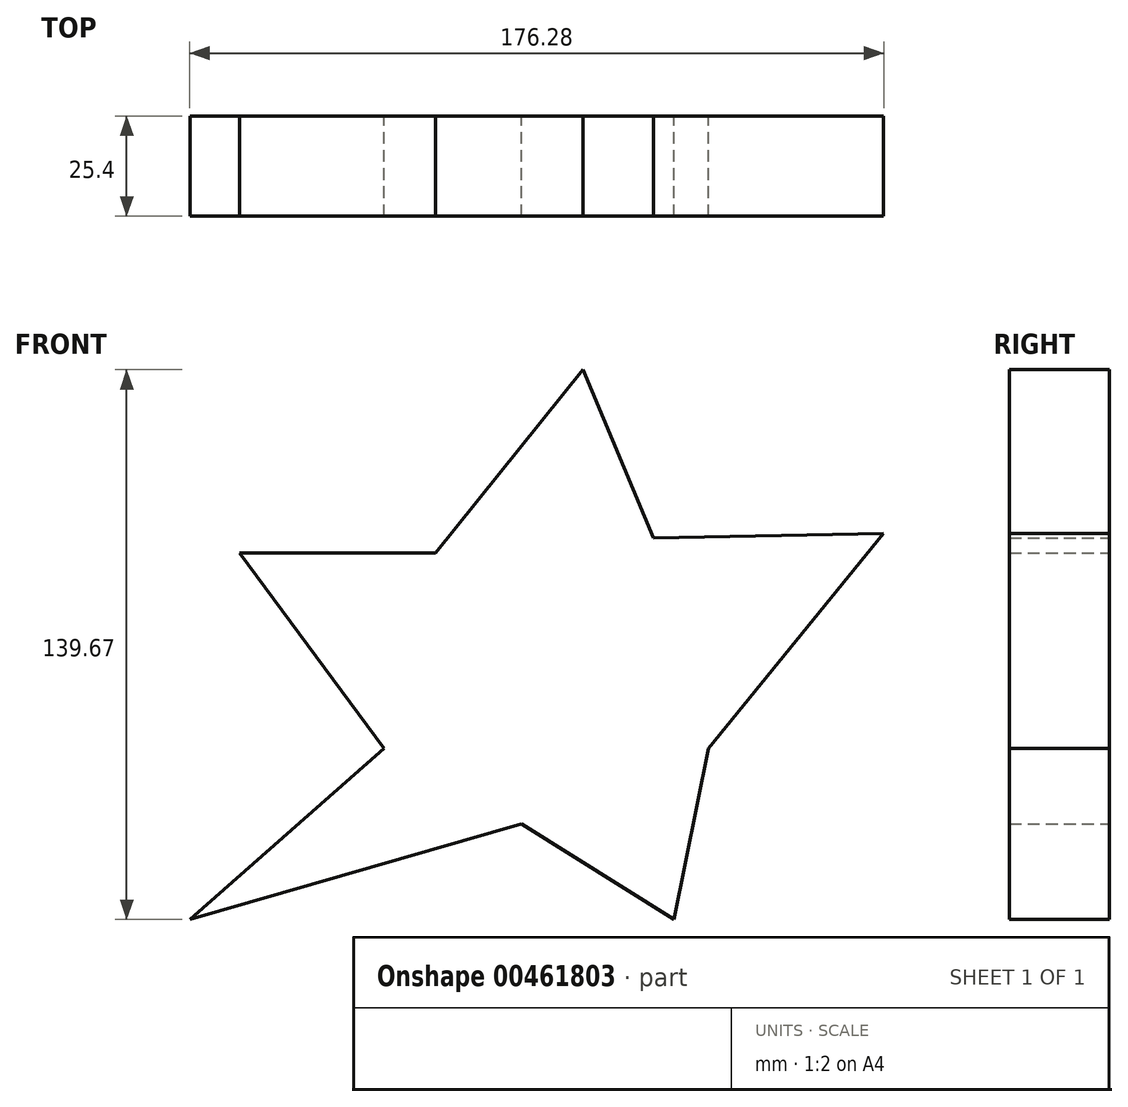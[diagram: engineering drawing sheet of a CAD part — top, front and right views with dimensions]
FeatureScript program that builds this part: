
annotation { "Feature Type Name" : "Feature", "Feature Type Description" : "" }
export const myFeature = defineFeature(function(context is Context, id is Id, definition is map)
    precondition{}
    {
        {
            var Q0;
            Q0=qCreatedBy(makeId("Front.planeOp"),FACE);
            var sketch = newSketch(context, id + "F0", { "sketchPlane" : qUnion([Q0])});
            skLineSegment(sketch, "E0", {"start": v(-36.87, 68.77) * mm, "end": v(-74.4, 22.16) * mm});
            skLineSegment(sketch, "E1", {"start": v(-74.4, 22.16) * mm, "end": v(-124.13, 22.16) * mm});
            skLineSegment(sketch, "E2", {"start": v(-124.13, 22.16) * mm, "end": v(-87.48, -27.44) * mm});
            skLineSegment(sketch, "E3", {"start": v(-87.48, -27.44) * mm, "end": v(-136.79, -70.9) * mm});
            skLineSegment(sketch, "E4", {"start": v(-136.79, -70.9) * mm, "end": v(-52.58, -46.6) * mm});
            skLineSegment(sketch, "E5", {"start": v(-52.58, -46.6) * mm, "end": v(-13.74, -70.9) * mm});
            skLineSegment(sketch, "E6", {"start": v(-13.74, -70.9) * mm, "end": v(-5.02, -27.44) * mm});
            skLineSegment(sketch, "E7", {"start": v(-5.02, -27.44) * mm, "end": v(39.49, 27.1) * mm});
            skLineSegment(sketch, "E8", {"start": v(-18.98, 25.94) * mm, "end": v(39.49, 27.1) * mm});
            skLineSegment(sketch, "E9", {"start": v(-18.98, 25.94) * mm, "end": v(-36.87, 68.77) * mm});
            skSolve(sketch);
        }
        {
            var Q0;
            Q0 = qSketchRegion(id + "F0", true);
            extrude(context, id + "F1", {"entities" : qUnion([Q0]), "depth" : 25.4 * mm});
        }
    });
